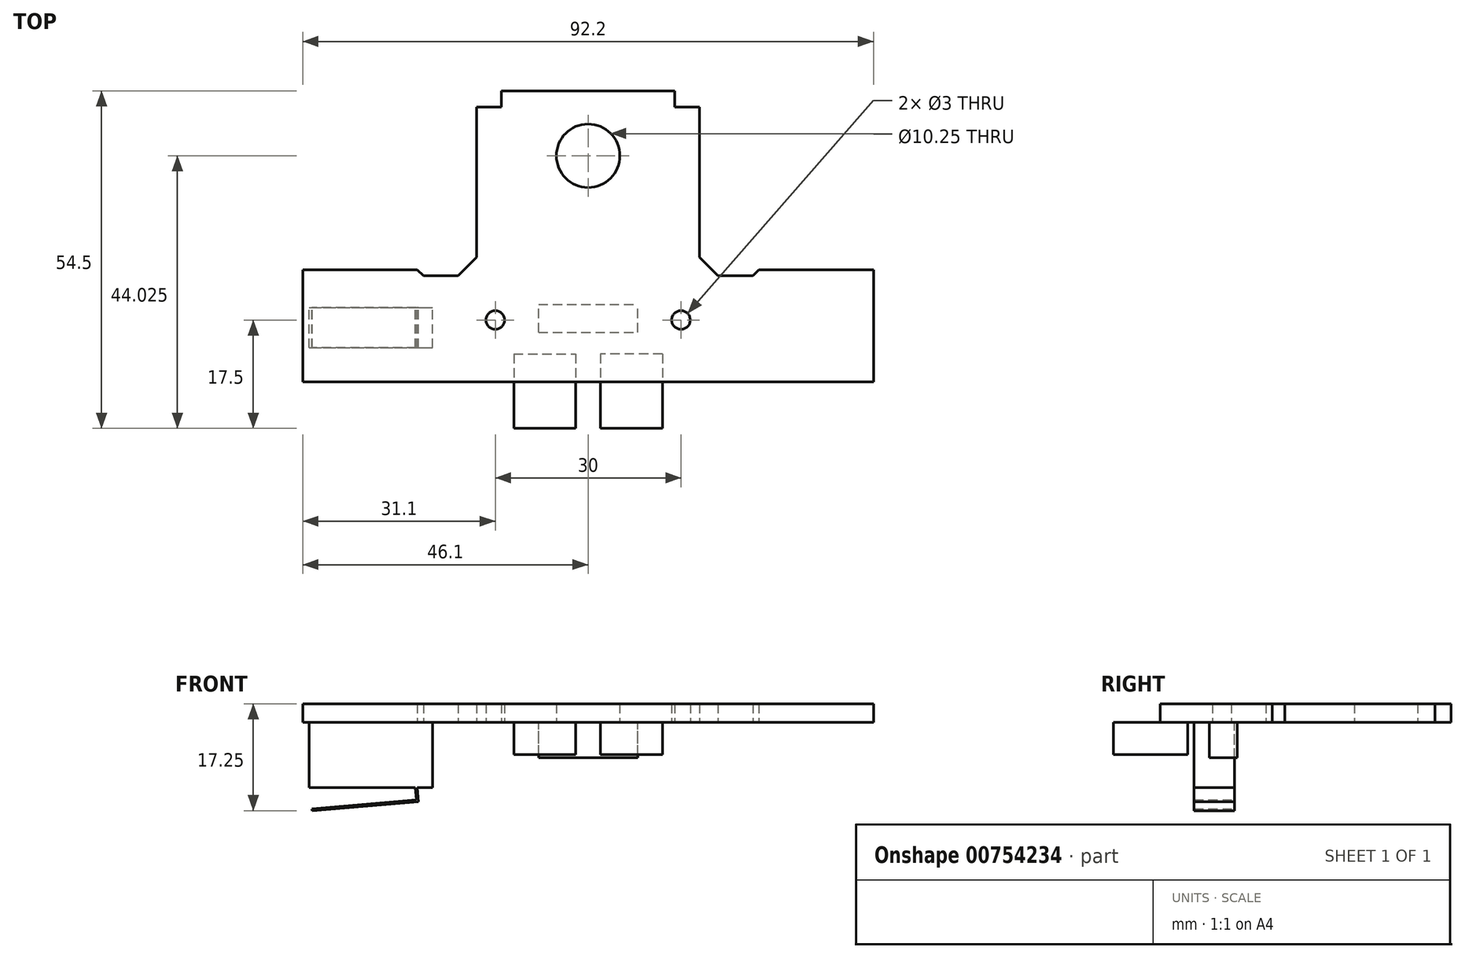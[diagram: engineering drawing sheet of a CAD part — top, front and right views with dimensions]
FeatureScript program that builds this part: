
annotation { "Feature Type Name" : "Feature", "Feature Type Description" : "" }
export const myFeature = defineFeature(function(context is Context, id is Id, definition is map)
    precondition{}
    {
        {
            var Q0;
            Q0=qCreatedBy(makeId("Top.planeOp"),FACE);
            var sketch = newSketch(context, id + "F0", { "sketchPlane" : qUnion([Q0])});
            skLineSegment(sketch, "E0", {"start": v(0, 0) * mm, "end": v(0, 36.52) * mm, "construction": true});
            skLineSegment(sketch, "E1", {"start": v(-46.1, 0) * mm, "end": v(46.1, 0) * mm});
            skCircle(sketch, "E2", {"center": v(0, 36.52) * mm, "radius": 5.13 * mm});
            skPoint(sketch, "E3", {"position": v(0, 31.4) * mm});
            skLineSegment(sketch, "E4", {"start": v(-46.1, 0) * mm, "end": v(-46.1, 18.13) * mm});
            skLineSegment(sketch, "E5", {"start": v(-46.1, 18.13) * mm, "end": v(-27.6, 18.13) * mm});
            skLineSegment(sketch, "E6", {"start": v(-27.6, 18.13) * mm, "end": v(-26.6, 17.13) * mm});
            skLineSegment(sketch, "E7", {"start": v(-26.6, 17.13) * mm, "end": v(-21, 17.13) * mm});
            skLineSegment(sketch, "E8", {"start": v(-21, 17.13) * mm, "end": v(-18, 20.13) * mm});
            skLineSegment(sketch, "E9", {"start": v(-18, 20.13) * mm, "end": v(-18, 44.4) * mm});
            skLineSegment(sketch, "E10", {"start": v(-18, 44.4) * mm, "end": v(-14, 44.4) * mm});
            skLineSegment(sketch, "E11", {"start": v(-14, 44.4) * mm, "end": v(-14, 47) * mm});
            skLineSegment(sketch, "E12", {"start": v(-14, 47) * mm, "end": v(14, 47) * mm});
            skLineSegment(sketch, "E13.MirrorCS", {"start": v(27.6, 18.13) * mm, "end": v(26.6, 17.13) * mm});
            skLineSegment(sketch, "E14.MirrorCS", {"start": v(26.6, 17.13) * mm, "end": v(21, 17.13) * mm});
            skLineSegment(sketch, "E15.MirrorCS", {"start": v(21, 17.13) * mm, "end": v(18, 20.13) * mm});
            skLineSegment(sketch, "E16.MirrorCS", {"start": v(14, 44.4) * mm, "end": v(14, 47) * mm});
            skLineSegment(sketch, "E17.MirrorCS", {"start": v(18, 44.4) * mm, "end": v(14, 44.4) * mm});
            skLineSegment(sketch, "E18.MirrorCS", {"start": v(18, 20.13) * mm, "end": v(18, 44.4) * mm});
            skLineSegment(sketch, "E19.MirrorCS", {"start": v(46.1, 18.13) * mm, "end": v(27.6, 18.13) * mm});
            skLineSegment(sketch, "E20.MirrorCS", {"start": v(46.1, 0) * mm, "end": v(46.1, 18.13) * mm});
            skCircle(sketch, "E21", {"center": v(-15, 10) * mm, "radius": 1.5 * mm});
            skCircle(sketch, "E22.MirrorC", {"center": v(15, 10) * mm, "radius": 1.5 * mm});
            skSolve(sketch);
        }
        {
            var Q0;
            Q0 = qSketchRegion(id + "F0", true);
            extrude(context, id + "F1", {"entities" : qUnion([Q0]), "depth" : 3 * mm, "offsetDistance" : 25 * mm});
        }
        {
            var Q0;
            Q0=makeQuery(id+"F1.opExtrude","CAP_FACE",FACE,{"disambiguationData":[OSD([sQuery(id+"F0.wireOp",EDGE,"E1"),sQuery(id+"F0.wireOp",EDGE,"E2"),sQuery(id+"F0.wireOp",EDGE,"E4"),sQuery(id+"F0.wireOp",EDGE,"E5"),sQuery(id+"F0.wireOp",EDGE,"E6"),sQuery(id+"F0.wireOp",EDGE,"E7"),sQuery(id+"F0.wireOp",EDGE,"E8"),sQuery(id+"F0.wireOp",EDGE,"E9"),sQuery(id+"F0.wireOp",EDGE,"E10"),sQuery(id+"F0.wireOp",EDGE,"E11"),sQuery(id+"F0.wireOp",EDGE,"E12"),sQuery(id+"F0.wireOp",EDGE,"E13.MirrorCS"),sQuery(id+"F0.wireOp",EDGE,"E14.MirrorCS"),sQuery(id+"F0.wireOp",EDGE,"E15.MirrorCS"),sQuery(id+"F0.wireOp",EDGE,"E16.MirrorCS"),sQuery(id+"F0.wireOp",EDGE,"E17.MirrorCS"),sQuery(id+"F0.wireOp",EDGE,"E18.MirrorCS"),sQuery(id+"F0.wireOp",EDGE,"E19.MirrorCS"),sQuery(id+"F0.wireOp",EDGE,"E20.MirrorCS")])],"isStart":true});
            var sketch = newSketch(context, id + "F2", { "sketchPlane" : qUnion([Q0])});
            skLineSegment(sketch, "E23.bottom", {"start": v(-45.1, -5.5) * mm, "end": v(-25.1, -5.5) * mm});
            skLineSegment(sketch, "E23.top", {"start": v(-45.1, -12) * mm, "end": v(-25.1, -12) * mm});
            skLineSegment(sketch, "E23.left", {"start": v(-45.1, -5.5) * mm, "end": v(-45.1, -12) * mm});
            skLineSegment(sketch, "E23.right", {"start": v(-25.1, -5.5) * mm, "end": v(-25.1, -12) * mm});
            skSolve(sketch);
        }
        {
            var Q0;
            Q0 = qSketchRegion(id + "F2", true);
            extrude(context, id + "F3", {"entities" : qUnion([Q0]), "operationType" : NewBodyOperationType.ADD, "depth" : 10.5 * mm, "offsetDistance" : 25 * mm});
        }
        {
            var Q0;
            Q0=makeQuery(id+"F3.opExtrude","SWEPT_FACE",FACE,{"disambiguationData":[OSD([sQuery(id+"F2.wireOp",EDGE,"E23.top")])]});
            var sketch = newSketch(context, id + "F4", { "sketchPlane" : qUnion([Q0])});
            skLineSegment(sketch, "E24", {"start": v(44.6, -13.95) * mm, "end": v(44.57, -14.25) * mm});
            skLineSegment(sketch, "E25", {"start": v(44.57, -14.25) * mm, "end": v(27.4, -12.8) * mm});
            skLineSegment(sketch, "E26", {"start": v(27.4, -12.8) * mm, "end": v(27.6, -10.5) * mm});
            skLineSegment(sketch, "E27", {"start": v(27.6, -10.5) * mm, "end": v(27.9, -10.5) * mm});
            skLineSegment(sketch, "E28", {"start": v(27.9, -10.5) * mm, "end": v(27.73, -12.53) * mm});
            skLineSegment(sketch, "E29", {"start": v(27.73, -12.53) * mm, "end": v(44.6, -13.95) * mm});
            skSolve(sketch);
        }
        {
            var Q0;
            Q0 = qSketchRegion(id + "F4", true);
            var Q1;
            Q1=makeQuery(id+"F3.opExtrude","CAP_VERTEX",VERTEX,{"disambiguationData":[OSD([sQuery(id+"F2.wireOp",EDGE,"E23.bottom"),sQuery(id+"F2.wireOp",EDGE,"E23.right")])],"isStart":false});
            extrude(context, id + "F5", {"entities" : qUnion([Q0]), "operationType" : NewBodyOperationType.ADD, "endBound" : BoundingType.UP_TO_VERTEX, "oppositeDirection" : true, "depth" : 25 * mm, "endBoundEntityVertex" : qUnion([Q1]), "offsetDistance" : 25 * mm});
        }
        {
            var Q0;
            Q0=makeQuery(id+"F1.opExtrude","CAP_FACE",FACE,{"disambiguationData":[OSD([sQuery(id+"F0.wireOp",EDGE,"E1"),sQuery(id+"F0.wireOp",EDGE,"E2"),sQuery(id+"F0.wireOp",EDGE,"E4"),sQuery(id+"F0.wireOp",EDGE,"E5"),sQuery(id+"F0.wireOp",EDGE,"E6"),sQuery(id+"F0.wireOp",EDGE,"E7"),sQuery(id+"F0.wireOp",EDGE,"E8"),sQuery(id+"F0.wireOp",EDGE,"E9"),sQuery(id+"F0.wireOp",EDGE,"E10"),sQuery(id+"F0.wireOp",EDGE,"E11"),sQuery(id+"F0.wireOp",EDGE,"E12"),sQuery(id+"F0.wireOp",EDGE,"E13.MirrorCS"),sQuery(id+"F0.wireOp",EDGE,"E14.MirrorCS"),sQuery(id+"F0.wireOp",EDGE,"E15.MirrorCS"),sQuery(id+"F0.wireOp",EDGE,"E16.MirrorCS"),sQuery(id+"F0.wireOp",EDGE,"E17.MirrorCS"),sQuery(id+"F0.wireOp",EDGE,"E18.MirrorCS"),sQuery(id+"F0.wireOp",EDGE,"E19.MirrorCS"),sQuery(id+"F0.wireOp",EDGE,"E20.MirrorCS")])],"isStart":true});
            var sketch = newSketch(context, id + "F6", { "sketchPlane" : qUnion([Q0])});
            skLineSegment(sketch, "E30.bottom", {"start": v(-8, -8) * mm, "end": v(8, -8) * mm});
            skLineSegment(sketch, "E30.top", {"start": v(-8, -12.5) * mm, "end": v(8, -12.5) * mm});
            skLineSegment(sketch, "E30.left", {"start": v(-8, -8) * mm, "end": v(-8, -12.5) * mm});
            skLineSegment(sketch, "E30.right", {"start": v(8, -8) * mm, "end": v(8, -12.5) * mm});
            skLineSegment(sketch, "E31", {"start": v(0, 0) * mm, "end": v(0, -31.4) * mm, "construction": true});
            skSolve(sketch);
        }
        {
            var Q0;
            Q0 = qSketchRegion(id + "F6", true);
            extrude(context, id + "F7", {"entities" : qUnion([Q0]), "operationType" : NewBodyOperationType.ADD, "depth" : 5.7 * mm, "offsetDistance" : 25 * mm});
        }
        {
            var Q0;
            Q0=makeQuery(id+"F1.opExtrude","CAP_FACE",FACE,{"disambiguationData":[OSD([sQuery(id+"F0.wireOp",EDGE,"E1"),sQuery(id+"F0.wireOp",EDGE,"E2"),sQuery(id+"F0.wireOp",EDGE,"E4"),sQuery(id+"F0.wireOp",EDGE,"E5"),sQuery(id+"F0.wireOp",EDGE,"E6"),sQuery(id+"F0.wireOp",EDGE,"E7"),sQuery(id+"F0.wireOp",EDGE,"E8"),sQuery(id+"F0.wireOp",EDGE,"E9"),sQuery(id+"F0.wireOp",EDGE,"E10"),sQuery(id+"F0.wireOp",EDGE,"E11"),sQuery(id+"F0.wireOp",EDGE,"E12"),sQuery(id+"F0.wireOp",EDGE,"E13.MirrorCS"),sQuery(id+"F0.wireOp",EDGE,"E14.MirrorCS"),sQuery(id+"F0.wireOp",EDGE,"E15.MirrorCS"),sQuery(id+"F0.wireOp",EDGE,"E16.MirrorCS"),sQuery(id+"F0.wireOp",EDGE,"E17.MirrorCS"),sQuery(id+"F0.wireOp",EDGE,"E18.MirrorCS"),sQuery(id+"F0.wireOp",EDGE,"E19.MirrorCS"),sQuery(id+"F0.wireOp",EDGE,"E20.MirrorCS")])],"isStart":true});
            var sketch = newSketch(context, id + "F8", { "sketchPlane" : qUnion([Q0])});
            skLineSegment(sketch, "E32.bottom", {"start": v(-12, -4.5) * mm, "end": v(-2, -4.5) * mm});
            skLineSegment(sketch, "E32.top", {"start": v(-12, 7.5) * mm, "end": v(-2, 7.5) * mm});
            skLineSegment(sketch, "E32.left", {"start": v(-12, -4.5) * mm, "end": v(-12, 7.5) * mm});
            skLineSegment(sketch, "E32.right", {"start": v(-2, -4.5) * mm, "end": v(-2, 7.5) * mm});
            skLineSegment(sketch, "E33", {"start": v(0, 0) * mm, "end": v(0, -36.52) * mm, "construction": true});
            skLineSegment(sketch, "E34.MirrorCS", {"start": v(12, 7.5) * mm, "end": v(2, 7.5) * mm});
            skLineSegment(sketch, "E35.MirrorCS", {"start": v(12, -4.5) * mm, "end": v(12, 7.5) * mm});
            skLineSegment(sketch, "E36.MirrorCS", {"start": v(12, -4.5) * mm, "end": v(2, -4.5) * mm});
            skLineSegment(sketch, "E37.MirrorCS", {"start": v(2, -4.5) * mm, "end": v(2, 7.5) * mm});
            skSolve(sketch);
        }
        {
            var Q0;
            Q0 = qSketchRegion(id + "F8", true);
            extrude(context, id + "F9", {"entities" : qUnion([Q0]), "operationType" : NewBodyOperationType.ADD, "depth" : 5.2 * mm, "offsetDistance" : 25 * mm});
        }
    });
